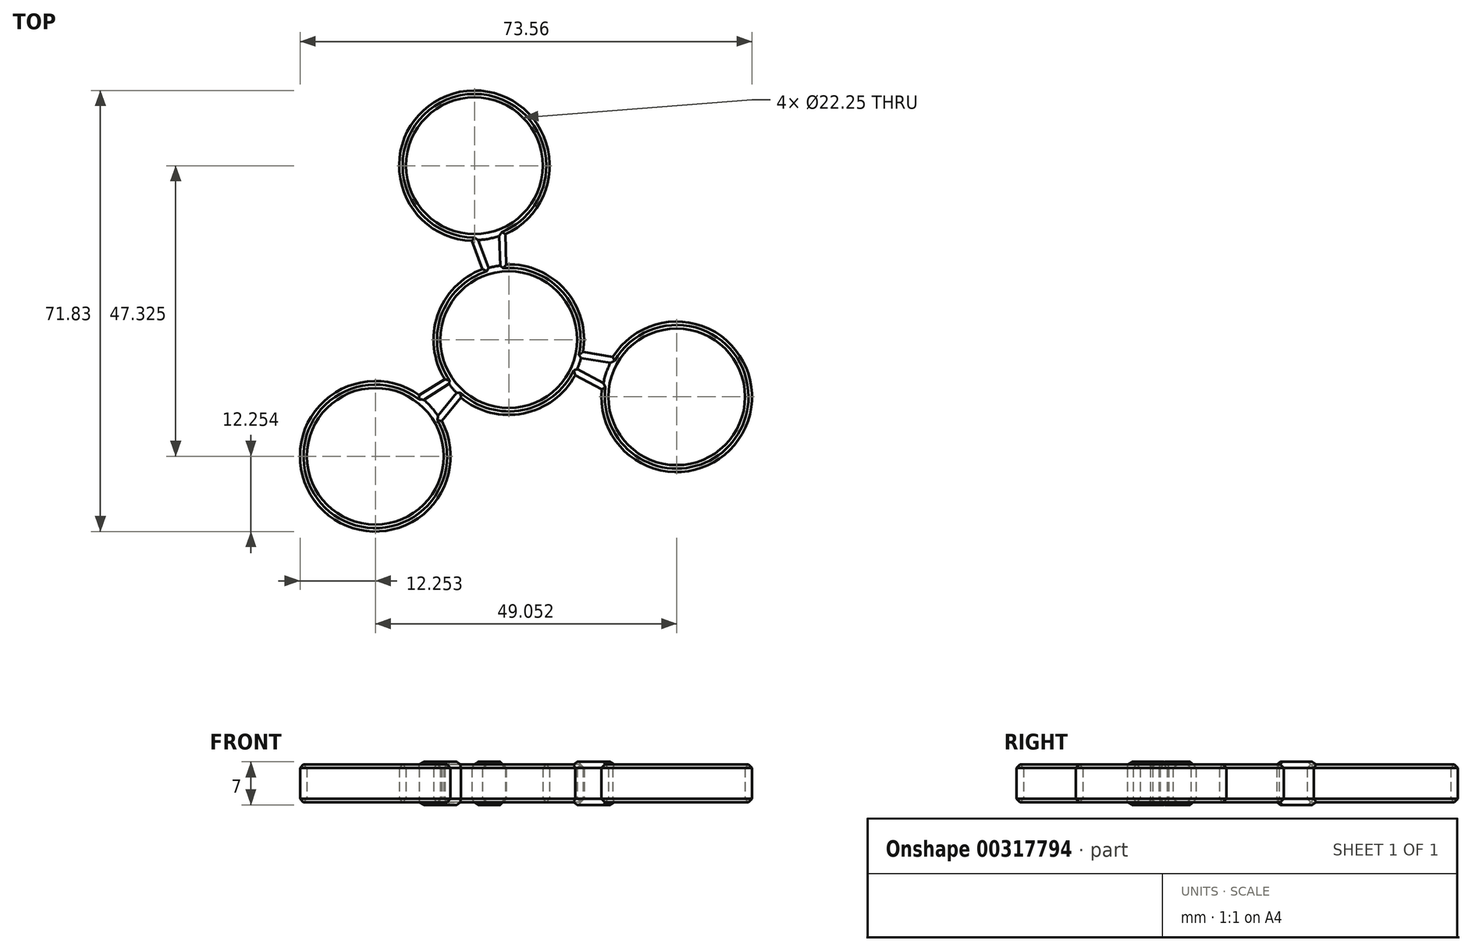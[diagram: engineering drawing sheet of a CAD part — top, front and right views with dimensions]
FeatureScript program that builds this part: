
annotation { "Feature Type Name" : "Feature", "Feature Type Description" : "" }
export const myFeature = defineFeature(function(context is Context, id is Id, definition is map)
    precondition{}
    {
        {
            var Q0;
            Q0=qCreatedBy(makeId("Top.planeOp"),FACE);
            var sketch = newSketch(context, id + "F0", { "sketchPlane" : qUnion([Q0])});
            skCircle(sketch, "E0", {"center": v(-24.62, 31.3) * mm, "radius": 11.12 * mm});
            skCircle(sketch, "E1", {"center": v(8.3, -6.34) * mm, "radius": 11.12 * mm});
            skCircle(sketch, "E2", {"center": v(-40.76, -16.03) * mm, "radius": 11.12 * mm});
            skLineSegment(sketch, "E3", {"start": v(-24.62, 31.3) * mm, "end": v(8.3, -6.34) * mm, "construction": true});
            skLineSegment(sketch, "E4", {"start": v(-40.76, -16.03) * mm, "end": v(8.3, -6.34) * mm, "construction": true});
            skLineSegment(sketch, "E5", {"start": v(-24.62, 31.3) * mm, "end": v(-40.76, -16.03) * mm, "construction": true});
            skLineSegment(sketch, "E6", {"start": v(-8.16, 12.48) * mm, "end": v(8.3, -6.34) * mm, "construction": true});
            skPoint(sketch, "E7", {"position": v(-19.03, 2.98) * mm});
            skCircle(sketch, "E8", {"center": v(-19.03, 2.98) * mm, "radius": 11.12 * mm});
            skPoint(sketch, "E9", {"position": v(-2.23, -2.75) * mm});
            skPoint(sketch, "E10", {"position": v(-2.81, -5.7) * mm});
            skPoint(sketch, "E11", {"position": v(-0.9, -0.06) * mm});
            skLineSegment(sketch, "E12", {"start": v(-0.9, -0.06) * mm, "end": v(-19.03, 2.98) * mm});
            skLineSegment(sketch, "E13", {"start": v(-2.81, -5.7) * mm, "end": v(-19.03, 2.98) * mm});
            skPoint(sketch, "E14", {"position": v(-22.47, 20.39) * mm});
            skPoint(sketch, "E15", {"position": v(-25.47, 20.2) * mm});
            skPoint(sketch, "E16", {"position": v(-19.63, 21.36) * mm});
            skLineSegment(sketch, "E17", {"start": v(-19.63, 21.36) * mm, "end": v(-19.03, 2.98) * mm});
            skLineSegment(sketch, "E18", {"start": v(-25.47, 20.2) * mm, "end": v(-19.03, 2.98) * mm});
            skPoint(sketch, "E19", {"position": v(-32.38, -8.7) * mm});
            skPoint(sketch, "E20", {"position": v(-34.64, -6.73) * mm});
            skPoint(sketch, "E21", {"position": v(-30.73, -11.2) * mm});
            skLineSegment(sketch, "E22", {"start": v(-19.03, 2.98) * mm, "end": v(-34.64, -6.73) * mm});
            skLineSegment(sketch, "E23", {"start": v(-30.73, -11.2) * mm, "end": v(-19.03, 2.98) * mm});
            skCircle(sketch, "E24", {"center": v(-19.03, 2.98) * mm, "radius": 12.25 * mm});
            skCircle(sketch, "E25", {"center": v(-24.62, 31.3) * mm, "radius": 12.25 * mm});
            skCircle(sketch, "E26", {"center": v(-40.76, -16.03) * mm, "radius": 12.25 * mm});
            skCircle(sketch, "E27", {"center": v(8.3, -6.34) * mm, "radius": 12.25 * mm});
            skCircle(sketch, "E28", {"center": v(-19.03, 2.98) * mm, "radius": 41.12 * mm, "construction": true});
            skSolve(sketch);
        }
        {
            var Q0;
            Q0 = qSketchRegion(id + "F0", true);
            extrude(context, id + "F1", {"entities" : qUnion([Q0]), "depth" : 7 * mm});
        }
        {
            var Q0;
            Q0=makeQuery(id+"F1.opExtrude","CAP_FACE",FACE,{"disambiguationData":[OSD([sQuery(id+"F0.wireOp",EDGE,"E0"),sQuery(id+"F0.wireOp",EDGE,"E1"),sQuery(id+"F0.wireOp",EDGE,"E2"),sQuery(id+"F0.wireOp",EDGE,"E8"),sQuery(id+"F0.wireOp",EDGE,"E12"),sQuery(id+"F0.wireOp",EDGE,"E13"),sQuery(id+"F0.wireOp",EDGE,"E17"),sQuery(id+"F0.wireOp",EDGE,"E18"),sQuery(id+"F0.wireOp",EDGE,"E22"),sQuery(id+"F0.wireOp",EDGE,"E23"),sQuery(id+"F0.wireOp",EDGE,"E24"),sQuery(id+"F0.wireOp",EDGE,"E25"),sQuery(id+"F0.wireOp",EDGE,"E26"),sQuery(id+"F0.wireOp",EDGE,"E27")])],"isStart":false});
            var Q1;
            Q1=makeQuery(id+"F1.opExtrude","CAP_FACE",FACE,{"disambiguationData":[OSD([sQuery(id+"F0.wireOp",EDGE,"E0"),sQuery(id+"F0.wireOp",EDGE,"E1"),sQuery(id+"F0.wireOp",EDGE,"E2"),sQuery(id+"F0.wireOp",EDGE,"E8"),sQuery(id+"F0.wireOp",EDGE,"E12"),sQuery(id+"F0.wireOp",EDGE,"E13"),sQuery(id+"F0.wireOp",EDGE,"E17"),sQuery(id+"F0.wireOp",EDGE,"E18"),sQuery(id+"F0.wireOp",EDGE,"E22"),sQuery(id+"F0.wireOp",EDGE,"E23"),sQuery(id+"F0.wireOp",EDGE,"E24"),sQuery(id+"F0.wireOp",EDGE,"E25"),sQuery(id+"F0.wireOp",EDGE,"E26"),sQuery(id+"F0.wireOp",EDGE,"E27")])],"isStart":true});
            chamfer(context, id + "F2", {"entities" : qUnion([Q0, Q1]), "width" : 1 * mm, "tangentPropagation" : true});
        }
    });
